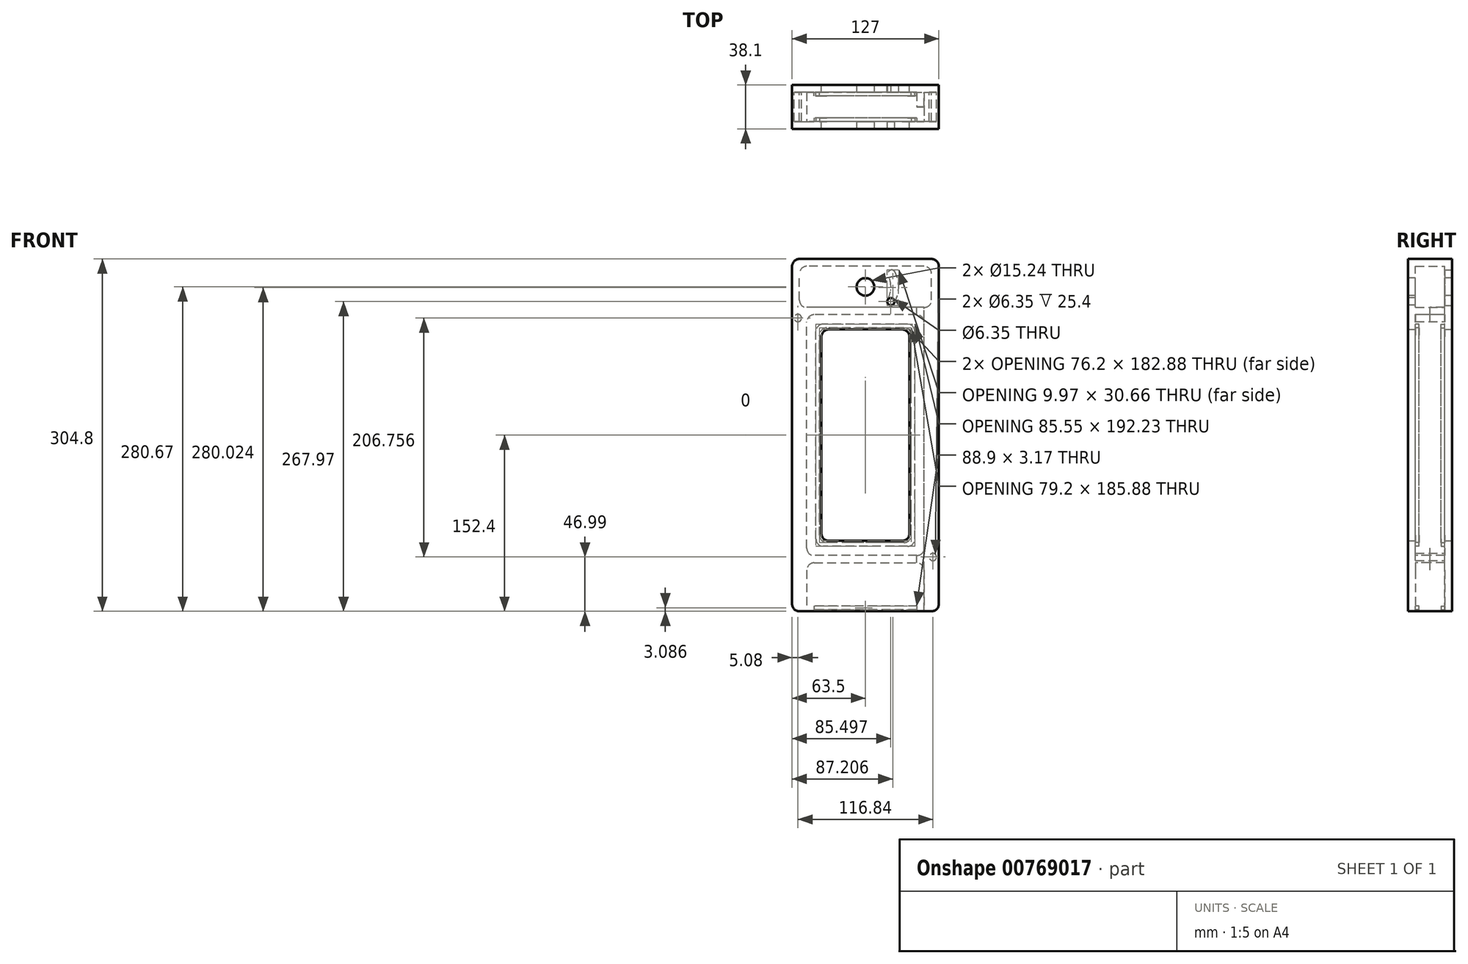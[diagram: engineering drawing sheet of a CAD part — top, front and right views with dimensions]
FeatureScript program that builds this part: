
annotation { "Feature Type Name" : "Feature", "Feature Type Description" : "" }
export const myFeature = defineFeature(function(context is Context, id is Id, definition is map)
    precondition{}
    {
        {
            var Q0;
            Q0=qCreatedBy(makeId("Front.planeOp"),FACE);
            var sketch = newSketch(context, id + "F0", { "sketchPlane" : qUnion([Q0])});
            skLineSegment(sketch, "E0.bottom", {"start": v(63.5, -152.4) * mm, "end": v(-63.5, -152.4) * mm});
            skLineSegment(sketch, "E0.top", {"start": v(63.5, 152.4) * mm, "end": v(-63.5, 152.4) * mm});
            skLineSegment(sketch, "E0.left", {"start": v(63.5, -152.4) * mm, "end": v(63.5, 152.4) * mm});
            skLineSegment(sketch, "E0.right", {"start": v(-63.5, -152.4) * mm, "end": v(-63.5, 152.4) * mm});
            skPoint(sketch, "E0.middle", {"position": v(0, 0) * mm});
            skLineSegment(sketch, "E1.bottom", {"start": v(38.1, -91.44) * mm, "end": v(-38.1, -91.44) * mm});
            skLineSegment(sketch, "E1.top", {"start": v(38.1, 91.44) * mm, "end": v(-38.1, 91.44) * mm});
            skLineSegment(sketch, "E1.left", {"start": v(38.1, -91.44) * mm, "end": v(38.1, 91.44) * mm});
            skLineSegment(sketch, "E1.right", {"start": v(-38.1, -91.44) * mm, "end": v(-38.1, 91.44) * mm});
            skSolve(sketch);
        }
        {
            var Q0;
            Q0=makeQuery(id+"F0.imprint","IMPRINT",FACE,{"disambiguationData":[TD([[makeQuery(id+"F0.imprint","IMPRINT",EDGE,{"derivedFrom":sQuery(id+"F0.wireOp",EDGE,"E0.bottom")}),-1.0]])]});
            extrude(context, id + "F1", {"entities" : qUnion([Q0]), "endBound" : BoundingType.SYMMETRIC, "depth" : 38.1 * mm, "offsetDistance" : 25.4 * mm});
        }
        {
            var Q0;
            Q0=makeQuery(id+"F1.opExtrude","SWEPT_FACE",FACE,{"disambiguationData":[OSD([sQuery(id+"F0.wireOp",EDGE,"E0.bottom")])]});
            var sketch = newSketch(context, id + "F2", { "sketchPlane" : qUnion([Q0])});
            skLineSegment(sketch, "E2.bottom", {"start": v(-50.8, -12.7) * mm, "end": v(50.8, -12.7) * mm});
            skLineSegment(sketch, "E2.top", {"start": v(-50.8, 12.7) * mm, "end": v(50.8, 12.7) * mm});
            skLineSegment(sketch, "E2.left", {"start": v(-50.8, -12.7) * mm, "end": v(-50.8, 12.7) * mm});
            skLineSegment(sketch, "E2.right", {"start": v(50.8, -12.7) * mm, "end": v(50.8, 12.7) * mm});
            skPoint(sketch, "E2.middle", {"position": v(0, 0) * mm});
            skSolve(sketch);
        }
        {
            var Q0;
            Q0=makeQuery(id+"F2.imprint","IMPRINT",FACE,{"disambiguationData":[TD([[makeQuery(id+"F2.imprint","IMPRINT",EDGE,{"derivedFrom":sQuery(id+"F2.wireOp",EDGE,"E2.bottom")}),1.0]])]});
            extrude(context, id + "F3", {"entities" : qUnion([Q0]), "operationType" : NewBodyOperationType.REMOVE, "oppositeDirection" : true, "depth" : 41.9 * mm, "offsetDistance" : 25.4 * mm});
        }
        {
            var Q0;
            Q0=qCreatedBy(makeId("Front.planeOp"),FACE);
            var sketch = newSketch(context, id + "F4", { "sketchPlane" : qUnion([Q0])});
            skLineSegment(sketch, "E3.bottom", {"start": v(50.8, -104.14) * mm, "end": v(-50.8, -104.14) * mm});
            skLineSegment(sketch, "E3.top", {"start": v(50.8, 104.14) * mm, "end": v(-50.8, 104.14) * mm});
            skLineSegment(sketch, "E3.left", {"start": v(50.8, -104.14) * mm, "end": v(50.8, 104.14) * mm});
            skLineSegment(sketch, "E3.right", {"start": v(-50.8, -104.14) * mm, "end": v(-50.8, 104.14) * mm});
            skPoint(sketch, "E3.middle", {"position": v(0, 0) * mm});
            skSolve(sketch);
        }
        {
            var Q0;
            Q0=makeQuery(id+"F4.imprint","IMPRINT",FACE,{"disambiguationData":[TD([[makeQuery(id+"F4.imprint","IMPRINT",EDGE,{"derivedFrom":sQuery(id+"F4.wireOp",EDGE,"E3.bottom")}),-1.0]])]});
            extrude(context, id + "F5", {"entities" : qUnion([Q0]), "operationType" : NewBodyOperationType.REMOVE, "endBound" : BoundingType.SYMMETRIC, "oppositeDirection" : true, "depth" : 25.4 * mm, "offsetDistance" : 25.4 * mm});
        }
        {
            var Q0;
            Q0=qCreatedBy(makeId("Front.planeOp"),FACE);
            var sketch = newSketch(context, id + "F6", { "sketchPlane" : qUnion([Q0])});
            skLineSegment(sketch, "E4.bottom", {"start": v(57.15, 110.49) * mm, "end": v(-57.15, 110.49) * mm});
            skLineSegment(sketch, "E4.top", {"start": v(57.15, 146.05) * mm, "end": v(-57.15, 146.05) * mm});
            skLineSegment(sketch, "E4.left", {"start": v(57.15, 110.5) * mm, "end": v(57.15, 146.05) * mm});
            skLineSegment(sketch, "E4.right", {"start": v(-57.15, 110.49) * mm, "end": v(-57.15, 146.05) * mm});
            skPoint(sketch, "E4.middle", {"position": v(0, 128.27) * mm});
            skSolve(sketch);
        }
        {
            var Q0;
            Q0 = qSketchRegion(id + "F6", true);
            extrude(context, id + "F7", {"entities" : qUnion([Q0]), "operationType" : NewBodyOperationType.REMOVE, "endBound" : BoundingType.SYMMETRIC, "depth" : 25.4 * mm, "offsetDistance" : 25.4 * mm});
        }
        {
            var Q0;
            Q0=makeQuery(id+"F5.boolean.opBoolean","COPY",FACE,{"derivedFrom":makeQuery(id+"F5.opExtrude","CAP_FACE",FACE,{"disambiguationData":[OSD([sQuery(id+"F4.wireOp",EDGE,"E3.bottom"),sQuery(id+"F4.wireOp",EDGE,"E3.top"),sQuery(id+"F4.wireOp",EDGE,"E3.left"),sQuery(id+"F4.wireOp",EDGE,"E3.right")])],"isStart":false})});
            var sketch = newSketch(context, id + "F8", { "sketchPlane" : qUnion([Q0])});
            skLineSegment(sketch, "E5.0", {"start": v(39.6, 92.94) * mm, "end": v(-39.6, 92.94) * mm});
            skLineSegment(sketch, "E5.1", {"start": v(39.6, -92.94) * mm, "end": v(39.6, 92.94) * mm});
            skLineSegment(sketch, "E5.2", {"start": v(39.6, -92.94) * mm, "end": v(-39.6, -92.94) * mm});
            skLineSegment(sketch, "E5.3", {"start": v(-39.6, -92.94) * mm, "end": v(-39.6, 92.94) * mm});
            skLineSegment(sketch, "E6.0", {"start": v(42.78, 96.12) * mm, "end": v(-42.77, 96.12) * mm});
            skLineSegment(sketch, "E6.1", {"start": v(42.77, -96.12) * mm, "end": v(42.78, 96.12) * mm});
            skLineSegment(sketch, "E6.2", {"start": v(42.77, -96.12) * mm, "end": v(-42.77, -96.12) * mm});
            skLineSegment(sketch, "E6.3", {"start": v(-42.77, -96.12) * mm, "end": v(-42.77, 96.12) * mm});
            skLineSegment(sketch, "E7.bottom", {"start": v(44.45, -147.73) * mm, "end": v(-44.45, -147.73) * mm});
            skLineSegment(sketch, "E7.top", {"start": v(44.45, -150.9) * mm, "end": v(-44.45, -150.9) * mm});
            skLineSegment(sketch, "E7.left", {"start": v(44.45, -147.73) * mm, "end": v(44.45, -150.9) * mm});
            skLineSegment(sketch, "E7.right", {"start": v(-44.45, -147.73) * mm, "end": v(-44.45, -150.9) * mm});
            skPoint(sketch, "E7.middle", {"position": v(0, -149.31) * mm});
            skSolve(sketch);
        }
        {
            var Q0;
            Q0 = qSketchRegion(id + "F8", true);
            extrude(context, id + "F9", {"entities" : qUnion([Q0]), "operationType" : NewBodyOperationType.ADD, "depth" : 3.17 * mm, "offsetDistance" : 25.4 * mm});
        }
        {
            var Q0;
            Q0=makeQuery(id+"F3.boolean.opBoolean","COPY",FACE,{"derivedFrom":makeQuery(id+"F3.opExtrude","SWEPT_FACE",FACE,{"disambiguationData":[OSD([sQuery(id+"F2.wireOp",EDGE,"E2.top")])]})});
            var sketch = newSketch(context, id + "F10", { "sketchPlane" : qUnion([Q0])});
            skLineSegment(sketch, "E8.0", {"start": v(-42.77, -96.12) * mm, "end": v(-42.78, 96.12) * mm});
            skLineSegment(sketch, "E9.0", {"start": v(-42.77, -96.12) * mm, "end": v(42.77, -96.12) * mm});
            skLineSegment(sketch, "E10.0", {"start": v(42.77, -96.12) * mm, "end": v(42.77, 96.12) * mm});
            skLineSegment(sketch, "E11.0", {"start": v(-42.78, 96.12) * mm, "end": v(42.77, 96.12) * mm});
            skLineSegment(sketch, "E12.0", {"start": v(-39.6, 92.94) * mm, "end": v(39.6, 92.94) * mm});
            skLineSegment(sketch, "E13.0", {"start": v(-39.6, -92.94) * mm, "end": v(-39.6, 92.94) * mm});
            skLineSegment(sketch, "E14.0", {"start": v(-39.6, -92.94) * mm, "end": v(39.6, -92.94) * mm});
            skLineSegment(sketch, "E15.0", {"start": v(39.6, -92.94) * mm, "end": v(39.6, 92.94) * mm});
            skPoint(sketch, "E16.orphan", {"position": v(-50.8, -110.5) * mm});
            skPoint(sketch, "E17.orphan", {"position": v(50.8, -110.5) * mm});
            skLineSegment(sketch, "E18.bottom", {"start": v(-44.45, -150.9) * mm, "end": v(44.45, -150.9) * mm});
            skLineSegment(sketch, "E18.top", {"start": v(-44.45, -147.73) * mm, "end": v(44.45, -147.73) * mm});
            skLineSegment(sketch, "E18.left", {"start": v(-44.45, -150.9) * mm, "end": v(-44.45, -147.73) * mm});
            skLineSegment(sketch, "E18.right", {"start": v(44.45, -150.9) * mm, "end": v(44.45, -147.73) * mm});
            skPoint(sketch, "E18.middle", {"position": v(0, -149.31) * mm});
            skSolve(sketch);
        }
        {
            var Q0;
            Q0 = qSketchRegion(id + "F10", true);
            extrude(context, id + "F11", {"entities" : qUnion([Q0]), "operationType" : NewBodyOperationType.ADD, "depth" : 3.17 * mm, "offsetDistance" : 25.4 * mm});
        }
        {
            var Q0;
            Q0=makeQuery(id+"F1.opExtrude","CAP_FACE",FACE,{"disambiguationData":[OSD([sQuery(id+"F0.wireOp",EDGE,"E0.bottom"),sQuery(id+"F0.wireOp",EDGE,"E0.top"),sQuery(id+"F0.wireOp",EDGE,"E0.left"),sQuery(id+"F0.wireOp",EDGE,"E0.right"),sQuery(id+"F0.wireOp",EDGE,"E1.bottom"),sQuery(id+"F0.wireOp",EDGE,"E1.top"),sQuery(id+"F0.wireOp",EDGE,"E1.left"),sQuery(id+"F0.wireOp",EDGE,"E1.right")])],"isStart":false});
            var sketch = newSketch(context, id + "F12", { "sketchPlane" : qUnion([Q0])});
            skPoint(sketch, "E19", {"position": v(0, 128.27) * mm});
            skSolve(sketch);
        }
        {
            var Q0;
            Q0=sQuery(id+"F12.wireOp",VERTEX,"E19");
            var Q1;
            Q1=makeQuery(id+"F1.opExtrude","SWEPT_BODY",BODY,{"disambiguationData":[OSD([sQuery(id+"F0.wireOp",EDGE,"E0.bottom"),sQuery(id+"F0.wireOp",EDGE,"E0.top"),sQuery(id+"F0.wireOp",EDGE,"E0.left"),sQuery(id+"F0.wireOp",EDGE,"E0.right"),sQuery(id+"F0.wireOp",EDGE,"E1.bottom"),sQuery(id+"F0.wireOp",EDGE,"E1.top"),sQuery(id+"F0.wireOp",EDGE,"E1.left"),sQuery(id+"F0.wireOp",EDGE,"E1.right")])]});
            hole(context, id + "F13", {"style" : HoleStyle.SIMPLE, "endStyle" : HoleEndStyle.THROUGH, "holeDiameter" : 15.24 * mm, "majorDiameter" : 6.35 * mm, "isTappedThrough" : true, "tappedDepth" : 12.7 * mm, "tapClearance" : 3, "locations" : qUnion([Q0]), "scope" : qUnion([Q1])});
        }
        {
            var Q0;
            Q0=makeQuery(id+"F7.boolean.opBoolean","COPY",EDGE,{"derivedFrom":makeQuery(id+"F7.opExtrude","SWEPT_EDGE",EDGE,{"disambiguationData":[OSD([sQuery(id+"F6.wireOp",EDGE,"E4.top"),sQuery(id+"F6.wireOp",EDGE,"E4.right")])]})});
            var Q1;
            Q1=makeQuery(id+"F7.boolean.opBoolean","COPY",EDGE,{"derivedFrom":makeQuery(id+"F7.opExtrude","SWEPT_EDGE",EDGE,{"disambiguationData":[OSD([sQuery(id+"F6.wireOp",EDGE,"E4.bottom"),sQuery(id+"F6.wireOp",EDGE,"E4.right")])]})});
            var Q2;
            Q2=makeQuery(id+"F7.boolean.opBoolean","COPY",EDGE,{"derivedFrom":makeQuery(id+"F7.opExtrude","SWEPT_EDGE",EDGE,{"disambiguationData":[OSD([sQuery(id+"F6.wireOp",EDGE,"E4.bottom"),sQuery(id+"F6.wireOp",EDGE,"E4.left")])]})});
            var Q3;
            Q3=makeQuery(id+"F7.boolean.opBoolean","COPY",EDGE,{"derivedFrom":makeQuery(id+"F7.opExtrude","SWEPT_EDGE",EDGE,{"disambiguationData":[OSD([sQuery(id+"F6.wireOp",EDGE,"E4.top"),sQuery(id+"F6.wireOp",EDGE,"E4.left")])]})});
            var Q4;
            Q4=makeQuery(id+"F5.boolean.opBoolean","COPY",EDGE,{"derivedFrom":makeQuery(id+"F5.opExtrude","SWEPT_EDGE",EDGE,{"disambiguationData":[OSD([sQuery(id+"F4.wireOp",EDGE,"E3.top"),sQuery(id+"F4.wireOp",EDGE,"E3.right")])]})});
            var Q5;
            Q5=makeQuery(id+"F5.boolean.opBoolean","COPY",EDGE,{"derivedFrom":makeQuery(id+"F5.opExtrude","SWEPT_EDGE",EDGE,{"disambiguationData":[OSD([sQuery(id+"F4.wireOp",EDGE,"E3.top"),sQuery(id+"F4.wireOp",EDGE,"E3.left")])]})});
            var Q6;
            Q6=makeQuery(id+"F3.boolean.opBoolean","COPY",EDGE,{"derivedFrom":makeQuery(id+"F3.opExtrude","CAP_EDGE",EDGE,{"disambiguationData":[OSD([sQuery(id+"F2.wireOp",EDGE,"E2.left")])],"isStart":false})});
            var Q7;
            Q7=makeQuery(id+"F5.boolean.opBoolean","COPY",EDGE,{"derivedFrom":makeQuery(id+"F5.opExtrude","SWEPT_EDGE",EDGE,{"disambiguationData":[OSD([sQuery(id+"F4.wireOp",EDGE,"E3.bottom"),sQuery(id+"F4.wireOp",EDGE,"E3.right")])]})});
            var Q8;
            Q8=makeQuery(id+"F3.boolean.opBoolean","COPY",EDGE,{"derivedFrom":makeQuery(id+"F3.opExtrude","CAP_EDGE",EDGE,{"disambiguationData":[OSD([sQuery(id+"F2.wireOp",EDGE,"E2.right")])],"isStart":false})});
            var Q9;
            Q9=makeQuery(id+"F5.boolean.opBoolean","COPY",EDGE,{"derivedFrom":makeQuery(id+"F5.opExtrude","SWEPT_EDGE",EDGE,{"disambiguationData":[OSD([sQuery(id+"F4.wireOp",EDGE,"E3.bottom"),sQuery(id+"F4.wireOp",EDGE,"E3.left")])]})});
            var Q10;
            Q10=makeQuery(id+"F11.opExtrude","SWEPT_EDGE",EDGE,{"disambiguationData":[OSD([sQuery(id+"F10.wireOp",EDGE,"E10.0"),sQuery(id+"F10.wireOp",EDGE,"E11.0")])]});
            var Q11;
            {var subQ0=sQuery(id+"F0.wireOp",EDGE,"E1.right");var subQ1=sQuery(id+"F0.wireOp",EDGE,"E1.top");Q11=makeQuery(id+"F5.boolean.opBoolean","SPLIT",EDGE,{"disambiguationData":[TD([makeQuery(id+"F5.opExtrude","CAP_FACE",FACE,{"disambiguationData":[OSD([sQuery(id+"F4.wireOp",EDGE,"E3.bottom"),sQuery(id+"F4.wireOp",EDGE,"E3.top"),sQuery(id+"F4.wireOp",EDGE,"E3.left"),sQuery(id+"F4.wireOp",EDGE,"E3.right")])],"isStart":true})])],"derivedFrom":makeQuery(id+"F1.opExtrude","SWEPT_EDGE",EDGE,{"disambiguationData":[OSD([subQ1,subQ0])]})});}
            var Q12;
            Q12=makeQuery(id+"F11.opExtrude","SWEPT_EDGE",EDGE,{"disambiguationData":[OSD([sQuery(id+"F10.wireOp",EDGE,"E12.0"),sQuery(id+"F10.wireOp",EDGE,"E15.0")])]});
            var Q13;
            {var subQ0=sQuery(id+"F0.wireOp",EDGE,"E1.left");var subQ1=sQuery(id+"F0.wireOp",EDGE,"E1.top");Q13=makeQuery(id+"F5.boolean.opBoolean","SPLIT",EDGE,{"disambiguationData":[TD([makeQuery(id+"F5.opExtrude","CAP_FACE",FACE,{"disambiguationData":[OSD([sQuery(id+"F4.wireOp",EDGE,"E3.bottom"),sQuery(id+"F4.wireOp",EDGE,"E3.top"),sQuery(id+"F4.wireOp",EDGE,"E3.left"),sQuery(id+"F4.wireOp",EDGE,"E3.right")])],"isStart":true})])],"derivedFrom":makeQuery(id+"F1.opExtrude","SWEPT_EDGE",EDGE,{"disambiguationData":[OSD([subQ1,subQ0])]})});}
            var Q14;
            Q14=makeQuery(id+"F11.opExtrude","SWEPT_EDGE",EDGE,{"disambiguationData":[OSD([sQuery(id+"F10.wireOp",EDGE,"E8.0"),sQuery(id+"F10.wireOp",EDGE,"E11.0")])]});
            var Q15;
            Q15=makeQuery(id+"F11.opExtrude","SWEPT_EDGE",EDGE,{"disambiguationData":[OSD([sQuery(id+"F10.wireOp",EDGE,"E12.0"),sQuery(id+"F10.wireOp",EDGE,"E13.0")])]});
            var Q16;
            Q16=makeQuery(id+"F9.opExtrude","SWEPT_EDGE",EDGE,{"disambiguationData":[OSD([sQuery(id+"F8.wireOp",EDGE,"E5.0"),sQuery(id+"F8.wireOp",EDGE,"E5.3")])]});
            var Q17;
            {var subQ0=sQuery(id+"F0.wireOp",EDGE,"E1.right");var subQ1=sQuery(id+"F0.wireOp",EDGE,"E1.top");Q17=makeQuery(id+"F5.boolean.opBoolean","SPLIT",EDGE,{"disambiguationData":[TD([makeQuery(id+"F5.opExtrude","CAP_FACE",FACE,{"disambiguationData":[OSD([sQuery(id+"F4.wireOp",EDGE,"E3.bottom"),sQuery(id+"F4.wireOp",EDGE,"E3.top"),sQuery(id+"F4.wireOp",EDGE,"E3.left"),sQuery(id+"F4.wireOp",EDGE,"E3.right")])],"isStart":false})])],"derivedFrom":makeQuery(id+"F1.opExtrude","SWEPT_EDGE",EDGE,{"disambiguationData":[OSD([subQ1,subQ0])]})});}
            var Q18;
            Q18=makeQuery(id+"F9.opExtrude","SWEPT_EDGE",EDGE,{"disambiguationData":[OSD([sQuery(id+"F8.wireOp",EDGE,"E6.0"),sQuery(id+"F8.wireOp",EDGE,"E6.3")])]});
            var Q19;
            Q19=makeQuery(id+"F9.opExtrude","SWEPT_EDGE",EDGE,{"disambiguationData":[OSD([sQuery(id+"F8.wireOp",EDGE,"E6.0"),sQuery(id+"F8.wireOp",EDGE,"E6.1")])]});
            var Q20;
            Q20=makeQuery(id+"F9.opExtrude","SWEPT_EDGE",EDGE,{"disambiguationData":[OSD([sQuery(id+"F8.wireOp",EDGE,"E5.0"),sQuery(id+"F8.wireOp",EDGE,"E5.1")])]});
            var Q21;
            {var subQ0=sQuery(id+"F0.wireOp",EDGE,"E1.left");var subQ1=sQuery(id+"F0.wireOp",EDGE,"E1.top");Q21=makeQuery(id+"F5.boolean.opBoolean","SPLIT",EDGE,{"disambiguationData":[TD([makeQuery(id+"F5.opExtrude","CAP_FACE",FACE,{"disambiguationData":[OSD([sQuery(id+"F4.wireOp",EDGE,"E3.bottom"),sQuery(id+"F4.wireOp",EDGE,"E3.top"),sQuery(id+"F4.wireOp",EDGE,"E3.left"),sQuery(id+"F4.wireOp",EDGE,"E3.right")])],"isStart":false})])],"derivedFrom":makeQuery(id+"F1.opExtrude","SWEPT_EDGE",EDGE,{"disambiguationData":[OSD([subQ1,subQ0])]})});}
            var Q22;
            {var subQ0=sQuery(id+"F0.wireOp",EDGE,"E1.left");var subQ1=sQuery(id+"F0.wireOp",EDGE,"E1.bottom");Q22=makeQuery(id+"F5.boolean.opBoolean","SPLIT",EDGE,{"disambiguationData":[TD([makeQuery(id+"F5.opExtrude","CAP_FACE",FACE,{"disambiguationData":[OSD([sQuery(id+"F4.wireOp",EDGE,"E3.bottom"),sQuery(id+"F4.wireOp",EDGE,"E3.top"),sQuery(id+"F4.wireOp",EDGE,"E3.left"),sQuery(id+"F4.wireOp",EDGE,"E3.right")])],"isStart":true})])],"derivedFrom":makeQuery(id+"F1.opExtrude","SWEPT_EDGE",EDGE,{"disambiguationData":[OSD([subQ1,subQ0])]})});}
            var Q23;
            {var subQ0=sQuery(id+"F0.wireOp",EDGE,"E1.left");var subQ1=sQuery(id+"F0.wireOp",EDGE,"E1.bottom");Q23=makeQuery(id+"F5.boolean.opBoolean","SPLIT",EDGE,{"disambiguationData":[TD([makeQuery(id+"F5.opExtrude","CAP_FACE",FACE,{"disambiguationData":[OSD([sQuery(id+"F4.wireOp",EDGE,"E3.bottom"),sQuery(id+"F4.wireOp",EDGE,"E3.top"),sQuery(id+"F4.wireOp",EDGE,"E3.left"),sQuery(id+"F4.wireOp",EDGE,"E3.right")])],"isStart":false})])],"derivedFrom":makeQuery(id+"F1.opExtrude","SWEPT_EDGE",EDGE,{"disambiguationData":[OSD([subQ1,subQ0])]})});}
            var Q24;
            Q24=makeQuery(id+"F9.opExtrude","SWEPT_EDGE",EDGE,{"disambiguationData":[OSD([sQuery(id+"F8.wireOp",EDGE,"E5.1"),sQuery(id+"F8.wireOp",EDGE,"E5.2")])]});
            var Q25;
            Q25=makeQuery(id+"F9.opExtrude","SWEPT_EDGE",EDGE,{"disambiguationData":[OSD([sQuery(id+"F8.wireOp",EDGE,"E6.1"),sQuery(id+"F8.wireOp",EDGE,"E6.2")])]});
            var Q26;
            Q26=makeQuery(id+"F11.opExtrude","SWEPT_EDGE",EDGE,{"disambiguationData":[OSD([sQuery(id+"F10.wireOp",EDGE,"E8.0"),sQuery(id+"F10.wireOp",EDGE,"E9.0")])]});
            var Q27;
            Q27=makeQuery(id+"F11.opExtrude","SWEPT_EDGE",EDGE,{"disambiguationData":[OSD([sQuery(id+"F10.wireOp",EDGE,"E13.0"),sQuery(id+"F10.wireOp",EDGE,"E14.0")])]});
            var Q28;
            Q28=makeQuery(id+"F9.opExtrude","SWEPT_EDGE",EDGE,{"disambiguationData":[OSD([sQuery(id+"F8.wireOp",EDGE,"E5.2"),sQuery(id+"F8.wireOp",EDGE,"E5.3")])]});
            var Q29;
            {var subQ0=sQuery(id+"F0.wireOp",EDGE,"E1.right");var subQ1=sQuery(id+"F0.wireOp",EDGE,"E1.bottom");Q29=makeQuery(id+"F5.boolean.opBoolean","SPLIT",EDGE,{"disambiguationData":[TD([makeQuery(id+"F5.opExtrude","CAP_FACE",FACE,{"disambiguationData":[OSD([sQuery(id+"F4.wireOp",EDGE,"E3.bottom"),sQuery(id+"F4.wireOp",EDGE,"E3.top"),sQuery(id+"F4.wireOp",EDGE,"E3.left"),sQuery(id+"F4.wireOp",EDGE,"E3.right")])],"isStart":false})])],"derivedFrom":makeQuery(id+"F1.opExtrude","SWEPT_EDGE",EDGE,{"disambiguationData":[OSD([subQ1,subQ0])]})});}
            var Q30;
            Q30=makeQuery(id+"F9.opExtrude","SWEPT_EDGE",EDGE,{"disambiguationData":[OSD([sQuery(id+"F8.wireOp",EDGE,"E6.2"),sQuery(id+"F8.wireOp",EDGE,"E6.3")])]});
            var Q31;
            Q31=makeQuery(id+"F11.opExtrude","SWEPT_EDGE",EDGE,{"disambiguationData":[OSD([sQuery(id+"F10.wireOp",EDGE,"E14.0"),sQuery(id+"F10.wireOp",EDGE,"E15.0")])]});
            var Q32;
            Q32=makeQuery(id+"F11.opExtrude","SWEPT_EDGE",EDGE,{"disambiguationData":[OSD([sQuery(id+"F10.wireOp",EDGE,"E9.0"),sQuery(id+"F10.wireOp",EDGE,"E10.0")])]});
            var Q33;
            {var subQ0=sQuery(id+"F0.wireOp",EDGE,"E1.right");var subQ1=sQuery(id+"F0.wireOp",EDGE,"E1.bottom");Q33=makeQuery(id+"F5.boolean.opBoolean","SPLIT",EDGE,{"disambiguationData":[TD([makeQuery(id+"F5.opExtrude","CAP_FACE",FACE,{"disambiguationData":[OSD([sQuery(id+"F4.wireOp",EDGE,"E3.bottom"),sQuery(id+"F4.wireOp",EDGE,"E3.top"),sQuery(id+"F4.wireOp",EDGE,"E3.left"),sQuery(id+"F4.wireOp",EDGE,"E3.right")])],"isStart":true})])],"derivedFrom":makeQuery(id+"F1.opExtrude","SWEPT_EDGE",EDGE,{"disambiguationData":[OSD([subQ1,subQ0])]})});}
            var Q34;
            Q34=makeQuery(id+"F1.opExtrude","SWEPT_EDGE",EDGE,{"disambiguationData":[OSD([sQuery(id+"F0.wireOp",EDGE,"E0.top"),sQuery(id+"F0.wireOp",EDGE,"E0.right")])]});
            var Q35;
            Q35=makeQuery(id+"F1.opExtrude","SWEPT_EDGE",EDGE,{"disambiguationData":[OSD([sQuery(id+"F0.wireOp",EDGE,"E0.top"),sQuery(id+"F0.wireOp",EDGE,"E0.left")])]});
            var Q36;
            Q36=makeQuery(id+"F1.opExtrude","SWEPT_EDGE",EDGE,{"disambiguationData":[OSD([sQuery(id+"F0.wireOp",EDGE,"E0.bottom"),sQuery(id+"F0.wireOp",EDGE,"E0.right")])]});
            var Q37;
            Q37=makeQuery(id+"F1.opExtrude","SWEPT_EDGE",EDGE,{"disambiguationData":[OSD([sQuery(id+"F0.wireOp",EDGE,"E0.bottom"),sQuery(id+"F0.wireOp",EDGE,"E0.left")])]});
            fillet(context, id + "F14", {"entities" : qUnion([Q0, Q1, Q2, Q3, Q4, Q5, Q6, Q7, Q8, Q9, Q10, Q11, Q12, Q13, Q14, Q15, Q16, Q17, Q18, Q19, Q20, Q21, Q22, Q23, Q24, Q25, Q26, Q27, Q28, Q29, Q30, Q31, Q32, Q33, Q34, Q35, Q36, Q37]), "radius" : 6.35 * mm, "tangentPropagation" : true, "allowEdgeOverflow" : false});
        }
        {
            var Q0;
            Q0=qCreatedBy(makeId("Front.planeOp"),FACE);
            var sketch = newSketch(context, id + "F15", { "sketchPlane" : qUnion([Q0])});
            skLineSegment(sketch, "E20.0", {"start": v(50.8, -125.48) * mm, "end": v(50.8, 116.84) * mm});
            skPoint(sketch, "E21.orphan", {"position": v(50.8, 97.8) * mm});
            skPoint(sketch, "E22.orphan", {"position": v(50.8, -97.8) * mm});
            skLineSegment(sketch, "E23.0", {"start": v(44.45, -125.48) * mm, "end": v(44.45, 116.84) * mm});
            skLineSegment(sketch, "E24", {"start": v(44.45, 116.84) * mm, "end": v(50.8, 116.84) * mm});
            skLineSegment(sketch, "E25", {"start": v(50.8, -125.48) * mm, "end": v(44.45, -125.48) * mm});
            skSolve(sketch);
        }
        {
            var Q0;
            Q0 = qSketchRegion(id + "F15", true);
            extrude(context, id + "F16", {"entities" : qUnion([Q0]), "operationType" : NewBodyOperationType.REMOVE, "oppositeDirection" : true, "depth" : 12.7 * mm, "offsetDistance" : 25.4 * mm});
        }
        {
            var Q0;
            Q0=makeQuery(id+"F1.opExtrude","CAP_FACE",FACE,{"disambiguationData":[OSD([sQuery(id+"F0.wireOp",EDGE,"E0.bottom"),sQuery(id+"F0.wireOp",EDGE,"E0.top"),sQuery(id+"F0.wireOp",EDGE,"E0.left"),sQuery(id+"F0.wireOp",EDGE,"E0.right"),sQuery(id+"F0.wireOp",EDGE,"E1.bottom"),sQuery(id+"F0.wireOp",EDGE,"E1.top"),sQuery(id+"F0.wireOp",EDGE,"E1.left"),sQuery(id+"F0.wireOp",EDGE,"E1.right")])],"isStart":true});
            var sketch = newSketch(context, id + "F17", { "sketchPlane" : qUnion([Q0])});
            skLineSegment(sketch, "E26", {"start": v(-39.52, 105.46) * mm, "end": v(0, 128.27) * mm, "construction": true});
            skLineSegment(sketch, "E27", {"start": v(0, 128.27) * mm, "end": v(-66.32, 161.53) * mm, "construction": true});
            skArc(sketch, "E28", {"start": v(-22.7, 139.66) * mm, "mid": v(-25.39, 127.52) * mm, "end": v(-22, 115.57) * mm, "construction": true});
            skArc(sketch, "E29.0", {"start": v(-25.66, 141.14) * mm, "mid": v(-28.69, 127.43) * mm, "end": v(-24.86, 113.92) * mm});
            skArc(sketch, "E30.0", {"start": v(-19.75, 138.18) * mm, "mid": v(-22.09, 127.62) * mm, "end": v(-19.14, 117.22) * mm});
            skLineSegment(sketch, "E31", {"start": v(-16.57, 128.27) * mm, "end": v(0, 128.27) * mm, "construction": true});
            skArc(sketch, "E32", {"start": v(-19.75, 138.18) * mm, "mid": v(-21.22, 142.6) * mm, "end": v(-25.66, 141.14) * mm});
            skArc(sketch, "E33", {"start": v(-19.14, 117.22) * mm, "mid": v(-20.35, 112.71) * mm, "end": v(-24.86, 113.92) * mm});
            skCircle(sketch, "E34.0", {"center": v(0, 128.27) * mm, "radius": 7.62 * mm, "construction": true});
            skSolve(sketch);
        }
        {
            var Q0;
            Q0 = qSketchRegion(id + "F17", true);
            extrude(context, id + "F18", {"entities" : qUnion([Q0]), "operationType" : NewBodyOperationType.REMOVE, "oppositeDirection" : true, "depth" : 25.4 * mm, "offsetDistance" : 25.4 * mm});
        }
        {
            var Q0;
            Q0=makeQuery(id+"F1.opExtrude","CAP_FACE",FACE,{"disambiguationData":[OSD([sQuery(id+"F0.wireOp",EDGE,"E0.bottom"),sQuery(id+"F0.wireOp",EDGE,"E0.top"),sQuery(id+"F0.wireOp",EDGE,"E0.left"),sQuery(id+"F0.wireOp",EDGE,"E0.right"),sQuery(id+"F0.wireOp",EDGE,"E1.bottom"),sQuery(id+"F0.wireOp",EDGE,"E1.top"),sQuery(id+"F0.wireOp",EDGE,"E1.left"),sQuery(id+"F0.wireOp",EDGE,"E1.right")])],"isStart":false});
            var sketch = newSketch(context, id + "F19", { "sketchPlane" : qUnion([Q0])});
            skCircle(sketch, "E35", {"center": v(22, 115.57) * mm, "radius": 3.18 * mm});
            skCircle(sketch, "E36.0", {"center": v(0, 128.27) * mm, "radius": 7.62 * mm, "construction": true});
            skSolve(sketch);
        }
        {
            var Q0;
            Q0 = qSketchRegion(id + "F19", true);
            extrude(context, id + "F20", {"entities" : qUnion([Q0]), "operationType" : NewBodyOperationType.REMOVE, "oppositeDirection" : true, "depth" : 12.7 * mm, "offsetDistance" : 25.4 * mm});
        }
        {
            var Q0;
            Q0=qCreatedBy(makeId("Front.planeOp"),FACE);
            var sketch = newSketch(context, id + "F21", { "sketchPlane" : qUnion([Q0])});
            skPoint(sketch, "E37", {"position": v(-58.42, 101.35) * mm});
            skPoint(sketch, "E38", {"position": v(58.42, -105.4) * mm});
            skCircle(sketch, "E39", {"center": v(-58.42, 101.35) * mm, "radius": 3.18 * mm});
            skCircle(sketch, "E40", {"center": v(58.42, -105.4) * mm, "radius": 3.18 * mm});
            skSolve(sketch);
        }
        {
            var Q0;
            Q0 = qSketchRegion(id + "F21", true);
            extrude(context, id + "F22", {"entities" : qUnion([Q0]), "operationType" : NewBodyOperationType.REMOVE, "endBound" : BoundingType.SYMMETRIC, "depth" : 25.4 * mm, "offsetDistance" : 25.4 * mm});
        }
    });
